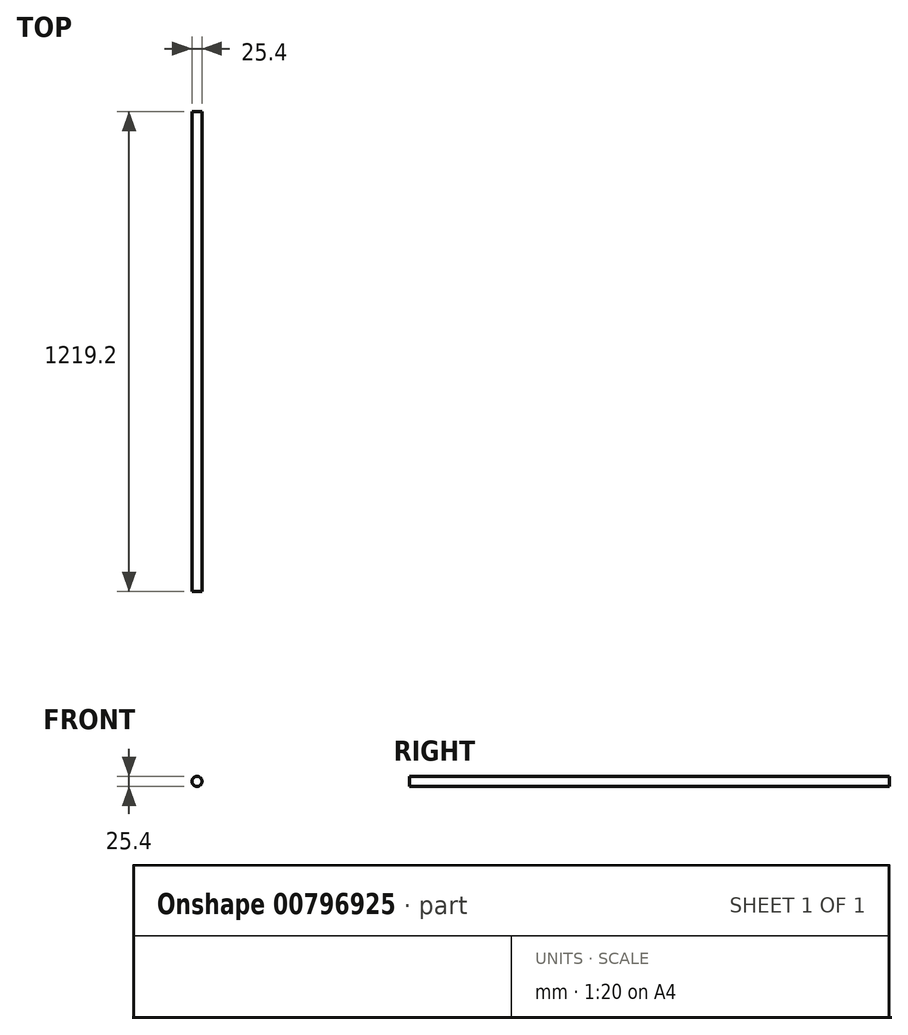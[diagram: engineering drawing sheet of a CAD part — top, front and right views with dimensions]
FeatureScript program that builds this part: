
annotation { "Feature Type Name" : "Feature", "Feature Type Description" : "" }
export const myFeature = defineFeature(function(context is Context, id is Id, definition is map)
    precondition{}
    {
        {
            var Q0;
            Q0=qCreatedBy(makeId("Front.planeOp"),FACE);
            var sketch = newSketch(context, id + "F0", { "sketchPlane" : qUnion([Q0])});
            skCircle(sketch, "E0", {"center": v(0, 0) * mm, "radius": 12.7 * mm});
            skSolve(sketch);
        }
        {
            var Q0;
            Q0 = qSketchRegion(id + "F0", true);
            extrude(context, id + "F1", {"entities" : qUnion([Q0]), "depth" : 609.6 * mm, "offsetDistance" : 25.4 * mm, "hasSecondDirection" : true, "secondDirectionOppositeDirection" : true, "secondDirectionDepth" : 609.6 * mm});
        }
    });
